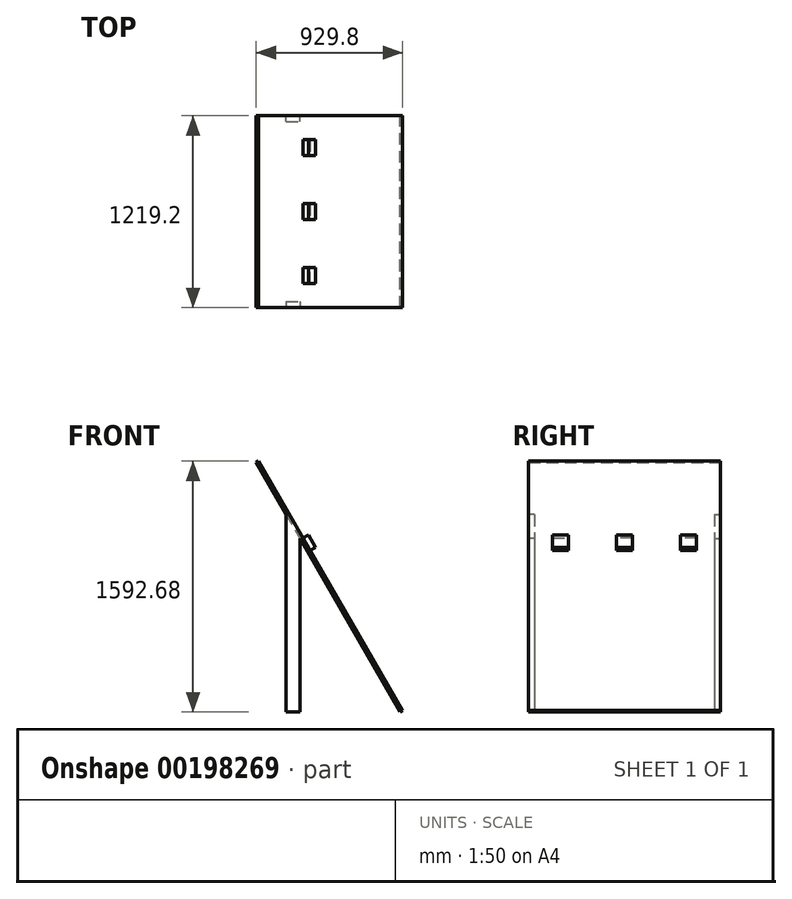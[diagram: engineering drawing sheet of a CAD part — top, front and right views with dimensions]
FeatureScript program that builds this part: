
annotation { "Feature Type Name" : "Feature", "Feature Type Description" : "" }
export const myFeature = defineFeature(function(context is Context, id is Id, definition is map)
    precondition{}
    {
        {
            var Q0;
            Q0=qCreatedBy(makeId("Front.planeOp"),FACE);
            var sketch = newSketch(context, id + "F0", { "sketchPlane" : qUnion([Q0])});
            skLineSegment(sketch, "E0", {"start": v(1428.02, 0) * mm, "end": v(-1552.53, 0) * mm});
            skLineSegment(sketch, "E1.bottom", {"start": v(1428.02, 8.9) * mm, "end": v(1412.62, 0) * mm});
            skLineSegment(sketch, "E1.top", {"start": v(818.42, 1064.75) * mm, "end": v(803.02, 1055.86) * mm});
            skLineSegment(sketch, "E1.left", {"start": v(1428.02, 8.9) * mm, "end": v(818.42, 1064.75) * mm});
            skLineSegment(sketch, "E1.right", {"start": v(1412.62, 0) * mm, "end": v(803.02, 1055.86) * mm});
            skLineSegment(sketch, "E2.top", {"start": v(513.62, 1592.68) * mm, "end": v(498.22, 1583.79) * mm});
            skLineSegment(sketch, "E2.left", {"start": v(818.42, 1064.75) * mm, "end": v(513.62, 1592.68) * mm});
            skLineSegment(sketch, "E2.right", {"start": v(803.02, 1055.86) * mm, "end": v(498.22, 1583.79) * mm});
            skSolve(sketch);
        }
        {
            var Q0;
            Q0=makeQuery(id+"F0.imprint","IMPRINT",FACE,{"disambiguationData":[TD([[makeQuery(id+"F0.imprint","IMPRINT",EDGE,{"derivedFrom":sQuery(id+"F0.wireOp",EDGE,"E1.bottom")}),-1.0]])]});
            extrude(context, id + "F1", {"entities" : qUnion([Q0]), "depth" : 1219.2 * mm});
        }
        {
            var Q0;
            Q0=makeQuery(id+"F0.imprint","IMPRINT",FACE,{"disambiguationData":[TD([[makeQuery(id+"F0.imprint","IMPRINT",EDGE,{"derivedFrom":sQuery(id+"F0.wireOp",EDGE,"E1.top")}),-1.0]])]});
            var Q1;
            Q1=makeQuery(id+"F1.opExtrude","CAP_FACE",FACE,{"disambiguationData":[OSD([sQuery(id+"F0.wireOp",EDGE,"E1.bottom"),sQuery(id+"F0.wireOp",EDGE,"E1.left"),sQuery(id+"F0.wireOp",EDGE,"E1.right"),sQuery(id+"F0.wireOp",EDGE,"E1.top")])],"isStart":false});
            extrude(context, id + "F2", {"entities" : qUnion([Q0]), "operationType" : NewBodyOperationType.ADD, "endBound" : BoundingType.UP_TO_SURFACE, "endBoundEntityFace" : qUnion([Q1]), "depth" : 1219.2 * mm});
        }
        {
            var Q0;
            Q0=qCreatedBy(makeId("Top.planeOp"),FACE);
            var sketch = newSketch(context, id + "F3", { "sketchPlane" : qUnion([Q0])});
            skLineSegment(sketch, "E3.bottom", {"start": v(777.62, 0) * mm, "end": v(688.72, 0) * mm});
            skLineSegment(sketch, "E3.top", {"start": v(777.62, -38.1) * mm, "end": v(688.72, -38.1) * mm});
            skLineSegment(sketch, "E3.left", {"start": v(777.62, 0) * mm, "end": v(777.62, -38.1) * mm});
            skLineSegment(sketch, "E3.right", {"start": v(688.72, 0) * mm, "end": v(688.72, -38.1) * mm});
            skLineSegment(sketch, "E4", {"start": v(1412.62, -609.6) * mm, "end": v(-877.33, -609.6) * mm});
            skLineSegment(sketch, "E5.MirrorCS", {"start": v(777.62, -1219.2) * mm, "end": v(777.62, -1181.1) * mm});
            skLineSegment(sketch, "E6.MirrorCS", {"start": v(688.72, -1219.2) * mm, "end": v(688.72, -1181.1) * mm});
            skLineSegment(sketch, "E7.MirrorCS", {"start": v(777.62, -1181.1) * mm, "end": v(688.72, -1181.1) * mm});
            skLineSegment(sketch, "E8.MirrorCS", {"start": v(777.62, -1219.2) * mm, "end": v(688.72, -1219.2) * mm});
            skLineSegment(sketch, "E9", {"start": v(1412.62, 0) * mm, "end": v(777.62, 0) * mm});
            skSolve(sketch);
        }
        {
            var Q0;
            Q0=makeQuery(id+"F3.imprint","IMPRINT",FACE,{"disambiguationData":[TD([[makeQuery(id+"F3.imprint","IMPRINT",EDGE,{"derivedFrom":sQuery(id+"F3.wireOp",EDGE,"E3.bottom")}),1.0]])]});
            var Q1;
            Q1=makeQuery(id+"F1.opExtrude","SWEPT_FACE",FACE,{"disambiguationData":[OSD([sQuery(id+"F0.wireOp",EDGE,"E1.right")])]});
            extrude(context, id + "F4", {"entities" : qUnion([Q0]), "operationType" : NewBodyOperationType.ADD, "endBound" : BoundingType.UP_TO_NEXT, "endBoundEntityFace" : qUnion([Q1]), "depth" : 25.4 * mm});
        }
        {
            var Q0;
            Q0 = qSketchRegion(id + "F3", true);
            extrude(context, id + "F5", {"entities" : qUnion([Q0]), "operationType" : NewBodyOperationType.ADD, "endBound" : BoundingType.UP_TO_NEXT, "depth" : 25.4 * mm});
        }
        {
            var Q0;
            Q0=makeQuery(id+"F2.boolean.opBoolean","MERGE",FACE,{"derivedFrom":[makeQuery(id+"F1.opExtrude","SWEPT_FACE",FACE,{"disambiguationData":[OSD([sQuery(id+"F0.wireOp",EDGE,"E1.left")])]}),makeQuery(id+"F2.opExtrude","SWEPT_FACE",FACE,{"disambiguationData":[OSD([sQuery(id+"F0.wireOp",EDGE,"E2.left")])]})]});
            var sketch = newSketch(context, id + "F6", { "sketchPlane" : qUnion([Q0])});
            skLineSegment(sketch, "E10", {"start": v(0, 512.89) * mm, "end": v(-1219.2, 512.89) * mm});
            skLineSegment(sketch, "E11.bottom", {"start": v(-152.4, 557.34) * mm, "end": v(-254, 557.34) * mm});
            skLineSegment(sketch, "E11.top", {"start": v(-152.4, 468.44) * mm, "end": v(-254, 468.44) * mm});
            skLineSegment(sketch, "E11.left", {"start": v(-152.4, 557.34) * mm, "end": v(-152.4, 468.44) * mm});
            skLineSegment(sketch, "E11.right", {"start": v(-254, 557.34) * mm, "end": v(-254, 468.44) * mm});
            skPoint(sketch, "E11.middle", {"position": v(-203.2, 512.89) * mm});
            skPoint(sketch, "E12", {"position": v(-609.6, 512.89) * mm});
            skLineSegment(sketch, "E13", {"start": v(-609.6, 512.89) * mm, "end": v(-609.6, 679.82) * mm});
            skLineSegment(sketch, "E14.MirrorCS", {"start": v(-1066.8, 557.34) * mm, "end": v(-965.2, 557.34) * mm});
            skLineSegment(sketch, "E15.MirrorCS", {"start": v(-1066.8, 557.34) * mm, "end": v(-1066.8, 468.44) * mm});
            skLineSegment(sketch, "E16.MirrorCS", {"start": v(-965.2, 557.34) * mm, "end": v(-965.2, 468.44) * mm});
            skLineSegment(sketch, "E17.MirrorCS", {"start": v(-1066.8, 468.44) * mm, "end": v(-965.2, 468.44) * mm});
            skPoint(sketch, "E18.MirrorP", {"position": v(-1016, 512.89) * mm});
            skLineSegment(sketch, "E19.bottom", {"start": v(-558.8, 557.34) * mm, "end": v(-660.4, 557.34) * mm});
            skLineSegment(sketch, "E19.top", {"start": v(-558.8, 468.44) * mm, "end": v(-660.4, 468.44) * mm});
            skLineSegment(sketch, "E19.left", {"start": v(-558.8, 557.34) * mm, "end": v(-558.8, 468.44) * mm});
            skLineSegment(sketch, "E19.right", {"start": v(-660.4, 557.34) * mm, "end": v(-660.4, 468.44) * mm});
            skSolve(sketch);
        }
        {
            var Q0;
            Q0 = qSketchRegion(id + "F6", true);
            extrude(context, id + "F7", {"entities" : qUnion([Q0]), "operationType" : NewBodyOperationType.ADD, "depth" : 38.1 * mm});
        }
    });
